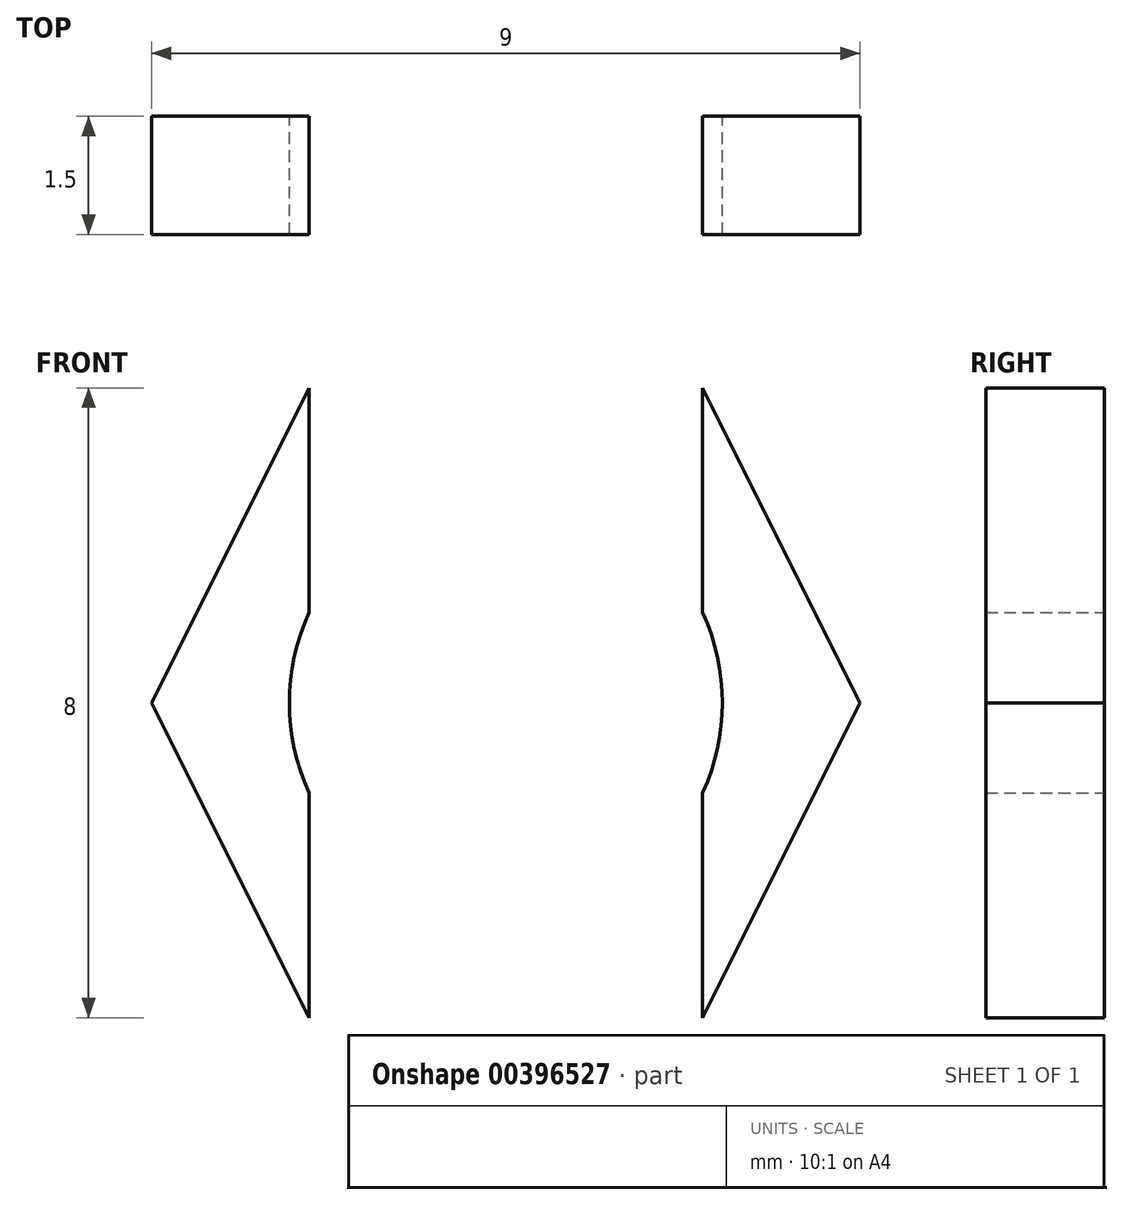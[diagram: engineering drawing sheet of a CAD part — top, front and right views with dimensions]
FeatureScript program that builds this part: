
annotation { "Feature Type Name" : "Feature", "Feature Type Description" : "" }
export const myFeature = defineFeature(function(context is Context, id is Id, definition is map)
    precondition{}
    {
        {
            var Q0;
            Q0=qCreatedBy(makeId("Front.planeOp"),FACE);
            var sketch = newSketch(context, id + "F0", { "sketchPlane" : qUnion([Q0])});
            skLineSegment(sketch, "E0.bottom", {"start": v(2.5, -4) * mm, "end": v(-2.5, -4) * mm});
            skLineSegment(sketch, "E0.top", {"start": v(2.5, 4) * mm, "end": v(-2.5, 4) * mm});
            skLineSegment(sketch, "E0.left", {"start": v(2.5, -4) * mm, "end": v(2.5, 4) * mm});
            skLineSegment(sketch, "E0.right", {"start": v(-2.5, -4) * mm, "end": v(-2.5, 4) * mm});
            skPoint(sketch, "E0.middle", {"position": v(0, 0) * mm});
            skCircle(sketch, "E1", {"center": v(0, 0) * mm, "radius": 2.75 * mm});
            skLineSegment(sketch, "E2", {"start": v(2.5, -4) * mm, "end": v(4.5, 0) * mm});
            skLineSegment(sketch, "E3", {"start": v(0, 0) * mm, "end": v(4.5, 0) * mm});
            skLineSegment(sketch, "E4", {"start": v(-2.5, -4) * mm, "end": v(-4.5, 0) * mm});
            skLineSegment(sketch, "E5", {"start": v(-4.5, 0) * mm, "end": v(0, 0) * mm});
            skLineSegment(sketch, "E6", {"start": v(-4.5, 0) * mm, "end": v(-2.5, 4) * mm});
            skLineSegment(sketch, "E7", {"start": v(2.5, 4) * mm, "end": v(4.5, 0) * mm});
            skLineSegment(sketch, "E8", {"start": v(0, -9.36) * mm, "end": v(0, 10.16) * mm});
            skSolve(sketch);
        }
        {
            var Q0;
            {var subQ0=sQuery(id+"F0.wireOp",EDGE,"E2");Q0=makeQuery(id+"F0.imprint","IMPRINT",FACE,{"disambiguationData":[TD([[makeQuery(id+"F0.imprint","IMPRINT",EDGE,{"derivedFrom":subQ0}),1.0]])]});}
            var Q1;
            {var subQ0=sQuery(id+"F0.wireOp",EDGE,"E0.left");var subQ5=sQuery(id+"F0.wireOp",EDGE,"E1");var subQ7=makeQuery(id+"F0.imprint","INTERSECT",VERTEX,{"disambiguationData":[OD(0.0)],"derivedFrom":[subQ0,subQ5]});Q1=makeQuery(id+"F0.imprint","IMPRINT",FACE,{"disambiguationData":[TD([[makeQuery(id+"F0.imprint","IMPRINT",EDGE,{"disambiguationData":[TD([[subQ7,1.0]])],"derivedFrom":subQ5}),-1.0]])]});}
            var Q2;
            {var subQ0=sQuery(id+"F0.wireOp",EDGE,"E0.right");var subQ5=sQuery(id+"F0.wireOp",EDGE,"E1");var subQ6=makeQuery(id+"F0.imprint","INTERSECT",VERTEX,{"disambiguationData":[OD(0.0)],"derivedFrom":[subQ0,subQ5]});Q2=makeQuery(id+"F0.imprint","IMPRINT",FACE,{"disambiguationData":[TD([[makeQuery(id+"F0.imprint","IMPRINT",EDGE,{"disambiguationData":[TD([[subQ6,-1.0]])],"derivedFrom":subQ5}),-1.0]])]});}
            var Q3;
            {var subQ0=sQuery(id+"F0.wireOp",EDGE,"E4");Q3=makeQuery(id+"F0.imprint","IMPRINT",FACE,{"disambiguationData":[TD([[makeQuery(id+"F0.imprint","IMPRINT",EDGE,{"derivedFrom":subQ0}),-1.0]])]});}
            var Q4;
            {var subQ0=sQuery(id+"F0.wireOp",EDGE,"E6");Q4=makeQuery(id+"F0.imprint","IMPRINT",FACE,{"disambiguationData":[TD([[makeQuery(id+"F0.imprint","IMPRINT",EDGE,{"derivedFrom":subQ0}),-1.0]])]});}
            var Q5;
            {var subQ0=sQuery(id+"F0.wireOp",EDGE,"E0.right");var subQ5=sQuery(id+"F0.wireOp",EDGE,"E1");var subQ7=makeQuery(id+"F0.imprint","INTERSECT",VERTEX,{"disambiguationData":[OD(1.0)],"derivedFrom":[subQ0,subQ5]});Q5=makeQuery(id+"F0.imprint","IMPRINT",FACE,{"disambiguationData":[TD([[makeQuery(id+"F0.imprint","IMPRINT",EDGE,{"disambiguationData":[TD([[subQ7,1.0]])],"derivedFrom":subQ5}),-1.0]])]});}
            var Q6;
            {var subQ0=sQuery(id+"F0.wireOp",EDGE,"E0.left");var subQ5=sQuery(id+"F0.wireOp",EDGE,"E1");var subQ6=makeQuery(id+"F0.imprint","INTERSECT",VERTEX,{"disambiguationData":[OD(1.0)],"derivedFrom":[subQ0,subQ5]});Q6=makeQuery(id+"F0.imprint","IMPRINT",FACE,{"disambiguationData":[TD([[makeQuery(id+"F0.imprint","IMPRINT",EDGE,{"disambiguationData":[TD([[subQ6,-1.0]])],"derivedFrom":subQ5}),-1.0]])]});}
            var Q7;
            {var subQ0=sQuery(id+"F0.wireOp",EDGE,"E7");Q7=makeQuery(id+"F0.imprint","IMPRINT",FACE,{"disambiguationData":[TD([[makeQuery(id+"F0.imprint","IMPRINT",EDGE,{"derivedFrom":subQ0}),-1.0]])]});}
            extrude(context, id + "F1", {"entities" : qUnion([Q0, Q1, Q2, Q3, Q4, Q5, Q6, Q7]), "depth" : 1.5 * mm});
        }
    });
